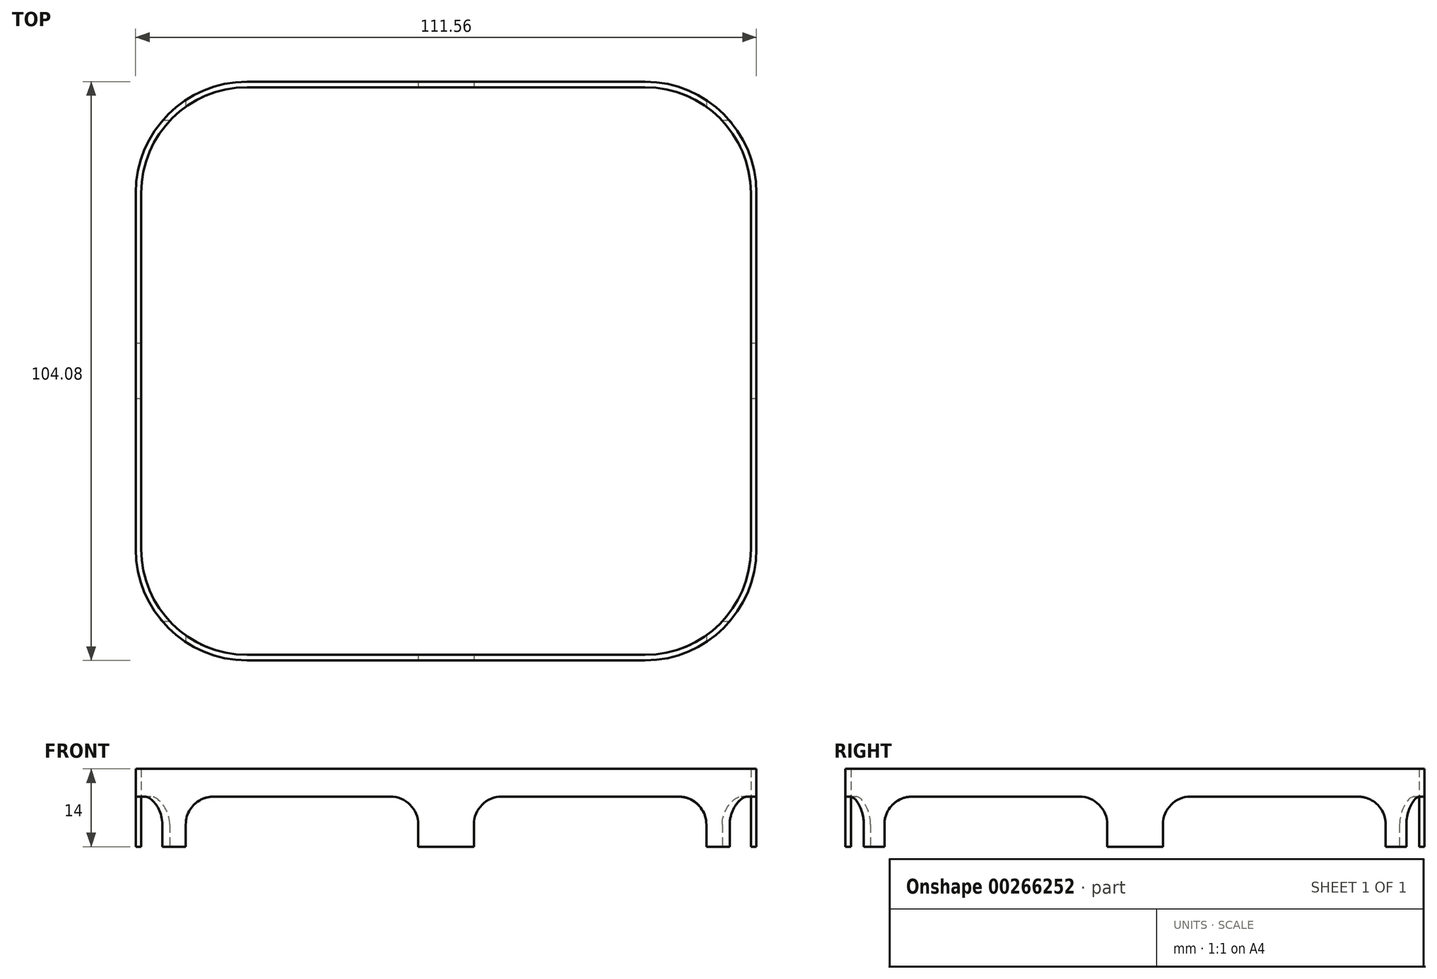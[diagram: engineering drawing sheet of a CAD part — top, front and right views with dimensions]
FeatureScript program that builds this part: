
annotation { "Feature Type Name" : "Feature", "Feature Type Description" : "" }
export const myFeature = defineFeature(function(context is Context, id is Id, definition is map)
    precondition{}
    {
        {
            var Q0;
            Q0=qCreatedBy(makeId("Top.planeOp"),FACE);
            var sketch = newSketch(context, id + "F0", { "sketchPlane" : qUnion([Q0])});
            skCircle(sketch, "E0", {"center": v(-29.78, 26.04) * mm, "radius": 24 * mm, "construction": true});
            skCircle(sketch, "E1", {"center": v(-29.78, -26.04) * mm, "radius": 24 * mm, "construction": true});
            skCircle(sketch, "E2", {"center": v(29.78, 26.04) * mm, "radius": 24 * mm, "construction": true});
            skCircle(sketch, "E3", {"center": v(29.78, -26.04) * mm, "radius": 24 * mm, "construction": true});
            skLineSegment(sketch, "E4", {"start": v(-20.28, 0) * mm, "end": v(0, 20.73) * mm, "construction": true});
            skLineSegment(sketch, "E5", {"start": v(0, 20.73) * mm, "end": v(20.28, 0) * mm, "construction": true});
            skLineSegment(sketch, "E6", {"start": v(20.28, 0) * mm, "end": v(0, -20.73) * mm, "construction": true});
            skLineSegment(sketch, "E7", {"start": v(0, -20.73) * mm, "end": v(-20.28, 0) * mm, "construction": true});
            skLineSegment(sketch, "E8", {"start": v(-55.78, 32.04) * mm, "end": v(-55.78, -32.04) * mm});
            skLineSegment(sketch, "E9", {"start": v(-35.78, -52.04) * mm, "end": v(35.78, -52.04) * mm});
            skLineSegment(sketch, "E10", {"start": v(55.78, -32.04) * mm, "end": v(55.78, 32.04) * mm});
            skLineSegment(sketch, "E11", {"start": v(35.78, 52.04) * mm, "end": v(-35.78, 52.04) * mm});
            skPoint(sketch, "E12.visualSharp", {"position": v(-55.78, 52.04) * mm});
            skArc(sketch, "E12.filletArc", {"start": v(-35.78, 52.04) * mm, "mid": v(-49.92, 46.19) * mm, "end": v(-55.78, 32.04) * mm});
            skPoint(sketch, "E13.visualSharp", {"position": v(-55.78, -52.04) * mm});
            skArc(sketch, "E13.filletArc", {"start": v(-55.78, -32.04) * mm, "mid": v(-49.92, -46.19) * mm, "end": v(-35.78, -52.04) * mm});
            skPoint(sketch, "E14.visualSharp", {"position": v(55.78, -52.04) * mm});
            skArc(sketch, "E14.filletArc", {"start": v(35.78, -52.04) * mm, "mid": v(49.92, -46.19) * mm, "end": v(55.78, -32.04) * mm});
            skPoint(sketch, "E15.visualSharp", {"position": v(55.78, 52.04) * mm});
            skArc(sketch, "E15.filletArc", {"start": v(55.78, 32.04) * mm, "mid": v(49.92, 46.19) * mm, "end": v(35.78, 52.04) * mm});
            skLineSegment(sketch, "E16.0", {"start": v(35.78, 51.04) * mm, "end": v(-35.78, 51.04) * mm});
            skArc(sketch, "E16.1", {"start": v(54.78, 32.04) * mm, "mid": v(49.21, 45.48) * mm, "end": v(35.78, 51.04) * mm});
            skArc(sketch, "E16.2", {"start": v(-35.78, 51.04) * mm, "mid": v(-49.21, 45.48) * mm, "end": v(-54.78, 32.04) * mm});
            skLineSegment(sketch, "E16.3", {"start": v(54.78, -32.04) * mm, "end": v(54.78, 32.04) * mm});
            skLineSegment(sketch, "E16.4", {"start": v(-54.78, 32.04) * mm, "end": v(-54.78, -32.04) * mm});
            skArc(sketch, "E16.5", {"start": v(-54.78, -32.04) * mm, "mid": v(-49.21, -45.48) * mm, "end": v(-35.78, -51.04) * mm});
            skLineSegment(sketch, "E16.6", {"start": v(-35.78, -51.04) * mm, "end": v(35.78, -51.04) * mm});
            skArc(sketch, "E16.7", {"start": v(35.78, -51.04) * mm, "mid": v(49.21, -45.48) * mm, "end": v(54.78, -32.04) * mm});
            skSolve(sketch);
        }
        {
            var Q0;
            Q0=makeQuery(id+"F0.imprint","IMPRINT",FACE,{"disambiguationData":[TD([[makeQuery(id+"F0.imprint","IMPRINT",EDGE,{"derivedFrom":sQuery(id+"F0.wireOp",EDGE,"E8")}),1.0]])]});
            extrude(context, id + "F1", {"entities" : qUnion([Q0]), "depth" : 14 * mm});
        }
        {
            var Q0;
            Q0=makeQuery(id+"F1.opExtrude","SWEPT_FACE",FACE,{"disambiguationData":[OSD([sQuery(id+"F0.wireOp",EDGE,"E9")])]});
            var sketch = newSketch(context, id + "F2", { "sketchPlane" : qUnion([Q0])});
            skLineSegment(sketch, "E17", {"start": v(-46.78, 0) * mm, "end": v(-46.78, 9) * mm});
            skLineSegment(sketch, "E18", {"start": v(46.78, 9) * mm, "end": v(46.78, 0) * mm});
            skLineSegment(sketch, "E19", {"start": v(-46.78, 9) * mm, "end": v(-5, 9) * mm});
            skLineSegment(sketch, "E20", {"start": v(-5, 9) * mm, "end": v(-5, 0) * mm});
            skLineSegment(sketch, "E21", {"start": v(-5, 0) * mm, "end": v(-46.78, 0) * mm});
            skLineSegment(sketch, "E22", {"start": v(46.78, 9) * mm, "end": v(5, 9) * mm});
            skLineSegment(sketch, "E23", {"start": v(5, 9) * mm, "end": v(5, 0) * mm});
            skLineSegment(sketch, "E24", {"start": v(5, 0) * mm, "end": v(46.78, 0) * mm});
            skSolve(sketch);
        }
        {
            var Q0;
            {var subQ0=sQuery(id+"F2.wireOp",EDGE,"E17");Q0=makeQuery(id+"F2.imprint","IMPRINT",FACE,{"disambiguationData":[TD([[makeQuery(id+"F2.imprint","IMPRINT",EDGE,{"derivedFrom":subQ0}),-1.0]])]});}
            var Q1;
            {var subQ0=sQuery(id+"F2.wireOp",EDGE,"E20");Q1=makeQuery(id+"F2.imprint","IMPRINT",FACE,{"disambiguationData":[TD([[makeQuery(id+"F2.imprint","IMPRINT",EDGE,{"derivedFrom":subQ0}),-1.0]])]});}
            var Q2;
            {var subQ0=sQuery(id+"F2.wireOp",EDGE,"E23");Q2=makeQuery(id+"F2.imprint","IMPRINT",FACE,{"disambiguationData":[TD([[makeQuery(id+"F2.imprint","IMPRINT",EDGE,{"derivedFrom":subQ0}),1.0]])]});}
            var Q3;
            {var subQ0=sQuery(id+"F2.wireOp",EDGE,"E18");Q3=makeQuery(id+"F2.imprint","IMPRINT",FACE,{"disambiguationData":[TD([[makeQuery(id+"F2.imprint","IMPRINT",EDGE,{"derivedFrom":subQ0}),-1.0]])]});}
            extrude(context, id + "F3", {"entities" : qUnion([Q0, Q1, Q2, Q3]), "operationType" : NewBodyOperationType.REMOVE, "endBound" : BoundingType.THROUGH_ALL, "oppositeDirection" : true, "depth" : 25 * mm});
        }
        {
            var Q0;
            Q0=makeQuery(id+"F1.opExtrude","SWEPT_FACE",FACE,{"disambiguationData":[OSD([sQuery(id+"F0.wireOp",EDGE,"E8")])]});
            var sketch = newSketch(context, id + "F4", { "sketchPlane" : qUnion([Q0])});
            skLineSegment(sketch, "E25", {"start": v(-45.04, 0) * mm, "end": v(-45.04, 9) * mm});
            skLineSegment(sketch, "E26", {"start": v(45.04, 9) * mm, "end": v(45.04, 0) * mm});
            skLineSegment(sketch, "E27", {"start": v(-45.04, 9) * mm, "end": v(-5, 9) * mm});
            skLineSegment(sketch, "E28", {"start": v(-5, 9) * mm, "end": v(-5, 0) * mm});
            skLineSegment(sketch, "E29", {"start": v(-5, 0) * mm, "end": v(-45.04, 0) * mm});
            skLineSegment(sketch, "E30", {"start": v(45.04, 9) * mm, "end": v(5, 9) * mm});
            skLineSegment(sketch, "E31", {"start": v(5, 9) * mm, "end": v(5, 0) * mm});
            skLineSegment(sketch, "E32", {"start": v(5, 0) * mm, "end": v(45.04, 0) * mm});
            skSolve(sketch);
        }
        {
            var Q0;
            {var subQ0=sQuery(id+"F4.wireOp",EDGE,"E25");Q0=makeQuery(id+"F4.imprint","IMPRINT",FACE,{"disambiguationData":[TD([[makeQuery(id+"F4.imprint","IMPRINT",EDGE,{"derivedFrom":subQ0}),-1.0]])]});}
            var Q1;
            {var subQ0=sQuery(id+"F4.wireOp",EDGE,"E28");Q1=makeQuery(id+"F4.imprint","IMPRINT",FACE,{"disambiguationData":[TD([[makeQuery(id+"F4.imprint","IMPRINT",EDGE,{"derivedFrom":subQ0}),-1.0]])]});}
            var Q2;
            {var subQ0=sQuery(id+"F4.wireOp",EDGE,"E31");Q2=makeQuery(id+"F4.imprint","IMPRINT",FACE,{"disambiguationData":[TD([[makeQuery(id+"F4.imprint","IMPRINT",EDGE,{"derivedFrom":subQ0}),1.0]])]});}
            var Q3;
            {var subQ0=sQuery(id+"F4.wireOp",EDGE,"E26");Q3=makeQuery(id+"F4.imprint","IMPRINT",FACE,{"disambiguationData":[TD([[makeQuery(id+"F4.imprint","IMPRINT",EDGE,{"derivedFrom":subQ0}),-1.0]])]});}
            extrude(context, id + "F5", {"entities" : qUnion([Q0, Q1, Q2, Q3]), "operationType" : NewBodyOperationType.REMOVE, "endBound" : BoundingType.THROUGH_ALL, "oppositeDirection" : true, "depth" : 25 * mm});
        }
        {
            var Q0;
            {var subQ0=sQuery(id+"F2.wireOp",EDGE,"E19");var subQ1=sQuery(id+"F2.wireOp",EDGE,"E20");Q0=makeQuery(id+"F3.boolean.opBoolean","COPY",EDGE,{"disambiguationData":[TD([makeQuery(id+"F1.opExtrude","SWEPT_FACE",FACE,{"disambiguationData":[OSD([sQuery(id+"F0.wireOp",EDGE,"E9")])]})])],"derivedFrom":makeQuery(id+"F3.opExtrude","SWEPT_EDGE",EDGE,{"disambiguationData":[OSD([subQ0,subQ1])]})});}
            var Q1;
            {var subQ0=sQuery(id+"F2.wireOp",EDGE,"E22");var subQ1=sQuery(id+"F2.wireOp",EDGE,"E23");Q1=makeQuery(id+"F3.boolean.opBoolean","COPY",EDGE,{"disambiguationData":[TD([makeQuery(id+"F1.opExtrude","SWEPT_FACE",FACE,{"disambiguationData":[OSD([sQuery(id+"F0.wireOp",EDGE,"E9")])]})])],"derivedFrom":makeQuery(id+"F3.opExtrude","SWEPT_EDGE",EDGE,{"disambiguationData":[OSD([subQ0,subQ1])]})});}
            var Q2;
            {var subQ0=sQuery(id+"F2.wireOp",EDGE,"E19");var subQ1=sQuery(id+"F2.wireOp",EDGE,"E20");Q2=makeQuery(id+"F3.boolean.opBoolean","COPY",EDGE,{"disambiguationData":[TD([makeQuery(id+"F1.opExtrude","SWEPT_FACE",FACE,{"disambiguationData":[OSD([sQuery(id+"F0.wireOp",EDGE,"E11")])]})])],"derivedFrom":makeQuery(id+"F3.opExtrude","SWEPT_EDGE",EDGE,{"disambiguationData":[OSD([subQ0,subQ1])]})});}
            var Q3;
            {var subQ0=sQuery(id+"F4.wireOp",EDGE,"E25");var subQ1=sQuery(id+"F4.wireOp",EDGE,"E27");Q3=makeQuery(id+"F5.boolean.opBoolean","COPY",EDGE,{"disambiguationData":[TD([makeQuery(id+"F1.opExtrude","SWEPT_FACE",FACE,{"disambiguationData":[OSD([sQuery(id+"F0.wireOp",EDGE,"E12.filletArc")])]})])],"derivedFrom":makeQuery(id+"F5.opExtrude","SWEPT_EDGE",EDGE,{"disambiguationData":[OSD([subQ0,subQ1])]})});}
            var Q4;
            {var subQ0=sQuery(id+"F2.wireOp",EDGE,"E19");var subQ1=sQuery(id+"F2.wireOp",EDGE,"E17");Q4=makeQuery(id+"F3.boolean.opBoolean","COPY",EDGE,{"disambiguationData":[TD([makeQuery(id+"F1.opExtrude","SWEPT_FACE",FACE,{"disambiguationData":[OSD([sQuery(id+"F0.wireOp",EDGE,"E12.filletArc")])]})])],"derivedFrom":makeQuery(id+"F3.opExtrude","SWEPT_EDGE",EDGE,{"disambiguationData":[OSD([subQ1,subQ0])]})});}
            var Q5;
            {var subQ0=sQuery(id+"F2.wireOp",EDGE,"E23");var subQ1=sQuery(id+"F2.wireOp",EDGE,"E22");Q5=makeQuery(id+"F3.boolean.opBoolean","COPY",EDGE,{"disambiguationData":[TD([makeQuery(id+"F1.opExtrude","SWEPT_FACE",FACE,{"disambiguationData":[OSD([sQuery(id+"F0.wireOp",EDGE,"E11")])]})])],"derivedFrom":makeQuery(id+"F3.opExtrude","SWEPT_EDGE",EDGE,{"disambiguationData":[OSD([subQ1,subQ0])]})});}
            var Q6;
            {var subQ0=sQuery(id+"F4.wireOp",EDGE,"E30");var subQ1=sQuery(id+"F4.wireOp",EDGE,"E26");Q6=makeQuery(id+"F5.boolean.opBoolean","COPY",EDGE,{"disambiguationData":[TD([makeQuery(id+"F1.opExtrude","SWEPT_FACE",FACE,{"disambiguationData":[OSD([sQuery(id+"F0.wireOp",EDGE,"E14.filletArc")])]})])],"derivedFrom":makeQuery(id+"F5.opExtrude","SWEPT_EDGE",EDGE,{"disambiguationData":[OSD([subQ1,subQ0])]})});}
            var Q7;
            {var subQ0=sQuery(id+"F2.wireOp",EDGE,"E18");var subQ1=sQuery(id+"F2.wireOp",EDGE,"E22");Q7=makeQuery(id+"F3.boolean.opBoolean","COPY",EDGE,{"disambiguationData":[TD([makeQuery(id+"F1.opExtrude","SWEPT_FACE",FACE,{"disambiguationData":[OSD([sQuery(id+"F0.wireOp",EDGE,"E14.filletArc")])]})])],"derivedFrom":makeQuery(id+"F3.opExtrude","SWEPT_EDGE",EDGE,{"disambiguationData":[OSD([subQ0,subQ1])]})});}
            var Q8;
            {var subQ0=sQuery(id+"F4.wireOp",EDGE,"E27");var subQ1=sQuery(id+"F4.wireOp",EDGE,"E28");Q8=makeQuery(id+"F5.boolean.opBoolean","COPY",EDGE,{"disambiguationData":[TD([makeQuery(id+"F1.opExtrude","SWEPT_FACE",FACE,{"disambiguationData":[OSD([sQuery(id+"F0.wireOp",EDGE,"E10")])]})])],"derivedFrom":makeQuery(id+"F5.opExtrude","SWEPT_EDGE",EDGE,{"disambiguationData":[OSD([subQ0,subQ1])]})});}
            var Q9;
            {var subQ0=sQuery(id+"F2.wireOp",EDGE,"E22");var subQ1=sQuery(id+"F2.wireOp",EDGE,"E18");Q9=makeQuery(id+"F3.boolean.opBoolean","COPY",EDGE,{"disambiguationData":[TD([makeQuery(id+"F1.opExtrude","SWEPT_FACE",FACE,{"disambiguationData":[OSD([sQuery(id+"F0.wireOp",EDGE,"E15.filletArc")])]})])],"derivedFrom":makeQuery(id+"F3.opExtrude","SWEPT_EDGE",EDGE,{"disambiguationData":[OSD([subQ1,subQ0])]})});}
            var Q10;
            {var subQ0=sQuery(id+"F4.wireOp",EDGE,"E25");var subQ1=sQuery(id+"F4.wireOp",EDGE,"E27");Q10=makeQuery(id+"F5.boolean.opBoolean","COPY",EDGE,{"disambiguationData":[TD([makeQuery(id+"F1.opExtrude","SWEPT_FACE",FACE,{"disambiguationData":[OSD([sQuery(id+"F0.wireOp",EDGE,"E15.filletArc")])]})])],"derivedFrom":makeQuery(id+"F5.opExtrude","SWEPT_EDGE",EDGE,{"disambiguationData":[OSD([subQ0,subQ1])]})});}
            var Q11;
            {var subQ0=sQuery(id+"F4.wireOp",EDGE,"E31");var subQ1=sQuery(id+"F4.wireOp",EDGE,"E30");Q11=makeQuery(id+"F5.boolean.opBoolean","COPY",EDGE,{"disambiguationData":[TD([makeQuery(id+"F1.opExtrude","SWEPT_FACE",FACE,{"disambiguationData":[OSD([sQuery(id+"F0.wireOp",EDGE,"E10")])]})])],"derivedFrom":makeQuery(id+"F5.opExtrude","SWEPT_EDGE",EDGE,{"disambiguationData":[OSD([subQ1,subQ0])]})});}
            var Q12;
            {var subQ0=sQuery(id+"F2.wireOp",EDGE,"E17");var subQ1=sQuery(id+"F2.wireOp",EDGE,"E19");Q12=makeQuery(id+"F3.boolean.opBoolean","COPY",EDGE,{"disambiguationData":[TD([makeQuery(id+"F1.opExtrude","SWEPT_FACE",FACE,{"disambiguationData":[OSD([sQuery(id+"F0.wireOp",EDGE,"E13.filletArc")])]})])],"derivedFrom":makeQuery(id+"F3.opExtrude","SWEPT_EDGE",EDGE,{"disambiguationData":[OSD([subQ0,subQ1])]})});}
            var Q13;
            {var subQ0=sQuery(id+"F4.wireOp",EDGE,"E31");var subQ1=sQuery(id+"F4.wireOp",EDGE,"E30");Q13=makeQuery(id+"F5.boolean.opBoolean","COPY",EDGE,{"disambiguationData":[TD([makeQuery(id+"F1.opExtrude","SWEPT_FACE",FACE,{"disambiguationData":[OSD([sQuery(id+"F0.wireOp",EDGE,"E8")])]})])],"derivedFrom":makeQuery(id+"F5.opExtrude","SWEPT_EDGE",EDGE,{"disambiguationData":[OSD([subQ1,subQ0])]})});}
            var Q14;
            {var subQ0=sQuery(id+"F4.wireOp",EDGE,"E26");var subQ1=sQuery(id+"F4.wireOp",EDGE,"E30");Q14=makeQuery(id+"F5.boolean.opBoolean","COPY",EDGE,{"disambiguationData":[TD([makeQuery(id+"F1.opExtrude","SWEPT_FACE",FACE,{"disambiguationData":[OSD([sQuery(id+"F0.wireOp",EDGE,"E13.filletArc")])]})])],"derivedFrom":makeQuery(id+"F5.opExtrude","SWEPT_EDGE",EDGE,{"disambiguationData":[OSD([subQ0,subQ1])]})});}
            var Q15;
            {var subQ0=sQuery(id+"F4.wireOp",EDGE,"E27");var subQ1=sQuery(id+"F4.wireOp",EDGE,"E28");Q15=makeQuery(id+"F5.boolean.opBoolean","COPY",EDGE,{"disambiguationData":[TD([makeQuery(id+"F1.opExtrude","SWEPT_FACE",FACE,{"disambiguationData":[OSD([sQuery(id+"F0.wireOp",EDGE,"E8")])]})])],"derivedFrom":makeQuery(id+"F5.opExtrude","SWEPT_EDGE",EDGE,{"disambiguationData":[OSD([subQ0,subQ1])]})});}
            fillet(context, id + "F6", {"entities" : qUnion([Q0, Q1, Q2, Q3, Q4, Q5, Q6, Q7, Q8, Q9, Q10, Q11, Q12, Q13, Q14, Q15]), "radius" : 5 * mm, "tangentPropagation" : true, "allowEdgeOverflow" : false});
        }
    });
